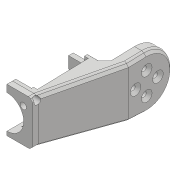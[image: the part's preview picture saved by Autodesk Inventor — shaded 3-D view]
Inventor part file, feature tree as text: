
AUTODESK INVENTOR PART (.ipt)
format: ipt  version: 2018 (Build 220112000, 112)  size: 933,888 bytes
history: native  units: mm
features: sketch x40, extrude x35, projected_geometry x33, hole x10, fillet x10, chamfer x10, mirror x1, plane x1
ambient origin geometry x8: Origin, YZ Plane, XZ Plane, XY Plane, X Axis, Y Axis, Z Axis, Center Point
bodies: Solid1 (feature_tree)
feature tree (140):
  extrude  "Extrusion1"  Depth=45.0mm
  extrude  "Extrusion2"  Depth=1.95mm
  hole  "Hole1"  [1 undecoded]
  hole  "Hole2"  [1 undecoded]
  fillet  "Fillet1"  Radius=14.0mm
  extrude  "Extrusion3"  Depth=18.5mm
  extrude  "Extrusion4"  Depth=10.0mm
  extrude  "Extrusion5"  Depth=2.0mm
  extrude  "Extrusion6"  Depth=2.0mm
  hole  "Hole3"  [1 undecoded]
  extrude  "Extrusion7"  Depth=2.0mm
  extrude  "Extrusion8"  Depth=5.0mm TaperAngle=0.0deg
  extrude  "Extrusion9"  Depth=10.0mm
  extrude  "Extrusion10"  Depth=10.0mm
  extrude  "Extrusion11"  Depth=21.0mm
  extrude  "Extrusion12"  Depth=14.5mm
  extrude  "Extrusion13"  Depth=5.0mm
  extrude  "Extrusion14"  Depth=2.25mm
  extrude  "Extrusion15"  Depth=5.0mm
  extrude  "Extrusion16"  Depth=9.0mm
  extrude  "Extrusion17"  Depth=4.0mm
  chamfer  "Chamfer1"  Distance=1.0mm
  fillet  "Fillet7"  Radius=20.7mm
  fillet  "Fillet8"  Radius=32.0mm
  mirror  "Mirror1"
  extrude  "Extrusion19"  Depth=1.0mm TaperAngle=0.0deg
  extrude  "Extrusion20"  Depth=8.0mm
  extrude  "Extrusion21"  Depth=0.2mm TaperAngle=0.0deg
  extrude  "Extrusion22"  Depth=21.0mm TaperAngle=0.0deg
  sketch  "Sketch29"  dims[d77=12.25mm d78=0.0mm d80=8.0mm]
  extrude  "Extrusion23"  Depth=5.0mm TaperAngle=0.0deg
  extrude  "Extrusion24"  Depth=0.2mm TaperAngle=0.0deg
  plane  "Work Plane1"
  extrude  "Extrusion25"  Depth=2.0mm TaperAngle=45.0deg
  extrude  "Extrusion26"  Depth=0.5mm
  extrude  "Extrusion27"  Depth=4.0mm
  extrude  "Extrusion28"  Depth=3.0mm TaperAngle=0.0deg
  extrude  "Extrusion29"  Depth=33.0mm
  extrude  "Extrusion30"  Depth=56.0mm
  extrude  "Extrusion31"  Depth=25.0mm TaperAngle=0.0deg
  chamfer  "Chamfer2"  Distance=6.0mm
  hole  "Hole6"  [1 undecoded]
  chamfer  "Chamfer3"  Distance=40.0mm
  extrude  "Extrusion32"  Depth=28.0mm
  extrude  "Extrusion33"  Depth=28.25mm
  chamfer  "Chamfer4"  Distance=12.0mm
  chamfer  "Chamfer5"  Distance=40.0mm
  chamfer  "Chamfer6"  Distance=40.0mm
  fillet  "Fillet9"  Radius=20.5mm
  extrude  "Extrusion34"  Depth=28.25mm TaperAngle=0.0deg
  chamfer  "Chamfer7"  Distance=20.5mm
  sketch  "Sketch42"  dims[d146=6.0mm d147=0.0mm d149=42.0mm]
  hole  "Hole7"  [1 undecoded]
  hole  "Hole8"  [1 undecoded]
  hole  "Hole9"  [1 undecoded]
  fillet  "Fillet10"  Radius=2.0mm
  chamfer  "Chamfer8"  Distance=7.0mm
  chamfer  "Chamfer9"  Distance=2.5mm
  fillet  "Fillet11"  Radius=7.0mm
  fillet  "Fillet12"  Radius=2.5mm
  extrude  "Extrusion35"  Depth=3.0mm TaperAngle=45.0deg
  sketch  "Sketch45"  dims[d151=4.5mm]
  hole  "Hole10"  [1 undecoded]
  hole  "Hole11"  [1 undecoded]
  hole  "Hole12"  [1 undecoded]
  fillet  "Fillet13"  Radius=12.0mm
  fillet  "Fillet14"  Radius=2.0mm
  fillet  "Fillet15"  Radius=15.0mm
  chamfer  "Chamfer10"  Distance=20.0mm
  extrude  "Extrusion36"  Depth=2.0mm TaperAngle=45.0deg
  sketch  "Sketch1"  dims[d0=24.5mm d1=45.0mm]
  sketch  "Sketch2"  dims[d2=1.95mm d3=0.0mm d4=2.25mm]
  projected_geometry  "Projected Loop1"
  sketch  "Sketch3"  dims[d5=20.0mm d6=2.25mm]
  projected_geometry  "Projected Loop2"
  sketch  "Sketch4"  dims[d7=5.25mm d8=5.25mm d9=14.0mm]
  projected_geometry  "Projected Loop3"
  sketch  "Sketch5"  dims[d10=5.25mm d11=18.5mm]
  projected_geometry  "Projected Loop4"
  sketch  "Sketch6"  dims[d12=10.0mm d13=0.0mm d14=20.5mm]
  projected_geometry  "Projected Loop5"
  sketch  "Sketch7"  dims[d15=2.0mm d16=2.195mm]
  projected_geometry  "Projected Loop6"
  sketch  "Sketch8"  dims[d17=2.0mm]
  projected_geometry  "Projected Loop7"
  sketch  "Sketch9"  dims[d18=2.4mm d19=6.0mm d20=4.4mm d21=2.0mm d22=90.0deg d23=8.0mm d24=20.594885mm d25=20.5mm]
  projected_geometry  "Projected Loop8"
  projected_geometry  "Projected Loop9"
  sketch  "Sketch10"  dims[d26=26.65mm d27=2.0mm]
  projected_geometry  "Projected Loop10"
  projected_geometry  "Projected Loop11"
  sketch  "Sketch11"  dims[d28=2.0mm]
  projected_geometry  "Projected Loop12"
  sketch  "Sketch12"  dims[d29=2.4mm d30=6.0mm d31=4.4mm d32=2.0mm d33=90.0deg d34=8.0mm d35=20.594885mm d36=0.5mm]
  sketch  "Sketch13"  dims[d37=18.0mm d38=5.0mm d39=0.0mm]
  sketch  "Sketch14"  dims[d41=10.0mm d42=0.0mm d43=24.5mm]
  projected_geometry  "Projected Loop13"
  sketch  "Sketch15"  dims[d44=1.15mm d45=0.0mm d46=10.0mm]
  sketch  "Sketch16"  dims[d47=21.0mm d48=14.5mm]
  projected_geometry  "Projected Loop14"
  sketch  "Sketch17"  dims[d49=20.0mm d50=14.5mm]
  projected_geometry  "Projected Loop15"
  sketch  "Sketch18"  dims[d51=24.5mm d52=5.0mm]
  projected_geometry  "Projected Loop16"
  sketch  "Sketch19"  dims[d53=5.0mm d54=2.25mm]
  projected_geometry  "Projected Loop17"
  sketch  "Sketch20"  dims[d55=2.25mm d56=5.0mm]
  projected_geometry  "Projected Loop18"
  sketch  "Sketch25"  dims[d57=5.0mm d58=9.0mm]
  projected_geometry  "Projected Loop22"
  sketch  "Sketch26"  dims[d59=14.75mm d60=4.0mm d61=1.0mm d62=0.0mm d63=20.7mm]
  sketch  "Sketch27"  dims[d64=2.4mm d65=6.0mm d66=4.4mm d67=2.0mm d68=90.0deg d69=8.0mm d70=20.594885mm d72=32.0mm]
  projected_geometry  "Projected Loop23"
  sketch  "Sketch28"  dims[d73=5.0mm d74=0.0mm d75=1.0mm d76=0.0mm]
  projected_geometry  "Projected Loop24"
  sketch  "Sketch31"  dims[d81=4.5mm d82=0.0mm d84=0.2mm d85=0.0mm]
  projected_geometry  "Projected Loop25"
  sketch  "Sketch32"  dims[d86=21.0mm d87=0.5mm d88=0.0mm]
  projected_geometry  "Projected Loop26"
  sketch  "Sketch33"  dims[d91=8.0mm d92=0.0mm d93=5.0mm d94=0.0mm]
  sketch  "Sketch34"  dims[d95=5.0mm d96=0.0mm d98=0.2mm d99=0.0mm]
  sketch  "Sketch35"  dims[d100=0.2mm d101=0.0mm d102=2.5mm d103=2.0mm d104=45.0deg]
  projected_geometry  "Projected Loop27"
  sketch  "Sketch36"  dims[d105=1.5mm d114=0.5mm]
  sketch  "Sketch37"  dims[d128=4.0mm d129=0.0mm d130=8.0mm]
  sketch  "Sketch38"  dims[d131=3.0mm d132=0.0mm d133=3.0mm d134=0.0mm]
  projected_geometry  "Projected Loop28"
  sketch  "Sketch39"  dims[d135=25.0mm d136=0.0mm d137=33.0mm]
  projected_geometry  "Projected Loop29"
  sketch  "Sketch40"  dims[d138=2.5mm d139=56.0mm]
  projected_geometry  "Projected Loop30"
  sketch  "Sketch41"  dims[d140=25.0mm d141=0.0mm d142=25.0mm d143=0.0mm d144=6.0mm d145=0.0mm]
  sketch  "Sketch44"  dims[d150=4.5mm]
  projected_geometry  "Projected Loop31"
  projected_geometry  "Projected Loop32"
  projected_geometry  "Projected Loop33"
  sketch  "Sketch46"  dims[d152=4.5mm d153=40.0mm d154=0.0mm d155=28.0mm d156=12.0mm d157=12.0mm d158=40.0mm d159=0.0mm d160=40.0mm d161=0.0mm d162=20.5mm d163=1.8mm d164=0.0mm d165=20.5mm d166=3.3mm d167=0.0mm d168=2.0mm d169=2.0mm d170=45.0deg d171=14.0mm d172=3.1mm d173=6.0mm d174=6.3mm d175=2.0mm d176=90.0deg d177=8.0mm d178=20.594885mm d179=1.2mm d180=2.0mm d181=45.0deg d182=7.0mm d183=2.5mm d184=0.0mm d185=7.0mm d186=2.5mm d187=0.0mm d188=3.0mm d189=15.0mm d190=45.0deg d191=3.0mm d192=15.0mm d193=45.0deg d194=3.0mm d195=15.0mm d196=45.0deg d197=2.0mm d198=12.0mm d199=2.0mm d200=15.0mm d201=20.0mm d202=0.0mm d203=2.0mm d204=15.0mm d205=45.0deg d206=2.9mm d207=2.9mm d208=3.18mm d209=3.18mm d210=4.0mm d211=6.0mm d212=6.3mm d213=2.0mm d214=90.0deg d215=8.0mm d216=20.594885mm d217=1.567mm d218=25.0mm d219=6.3mm d220=2.0mm d221=90.0deg d222=25.0mm d223=20.594885mm d224=2.15mm d225=20.0mm d226=4.4mm d227=2.0mm d228=90.0deg d229=10.0mm d230=0.0mm d231=0.5mm d232=2.0mm d233=15.0mm d234=45.0deg d235=2.0mm d236=15.0mm d237=45.0deg d238=1.0mm d239=3.0mm d240=3.9mm d241=3.9mm d242=3.5mm d243=0.0mm d244=2.75mm d245=2.75mm d246=2.5mm d247=1.567mm d248=4.0mm d249=4.4mm d250=2.0mm d251=90.0deg d252=40.0mm d253=20.594885mm d254=2.1mm d255=4.0mm d256=4.4mm d257=2.0mm d258=90.0deg d259=28.25mm d260=0.0mm d261=3.9mm d262=4.0mm d263=4.4mm d264=2.0mm d265=90.0deg d266=20.0mm d267=0.0mm d268=0.2mm d269=2.0mm d270=2.0mm d271=1.8mm d272=15.0mm d273=45.0deg d274=28.25mm d275=0.0mm]
  projected_geometry  "Project Cut Edges1"
  projected_geometry  "Project Cut Edges2"
  projected_geometry  "Project Cut Edges3"
note: 10 required parameter values undecoded (feature->parameter linkage not recoverable at this tier; creation-order binding heuristic only, values carry confidence <= 0.55)
